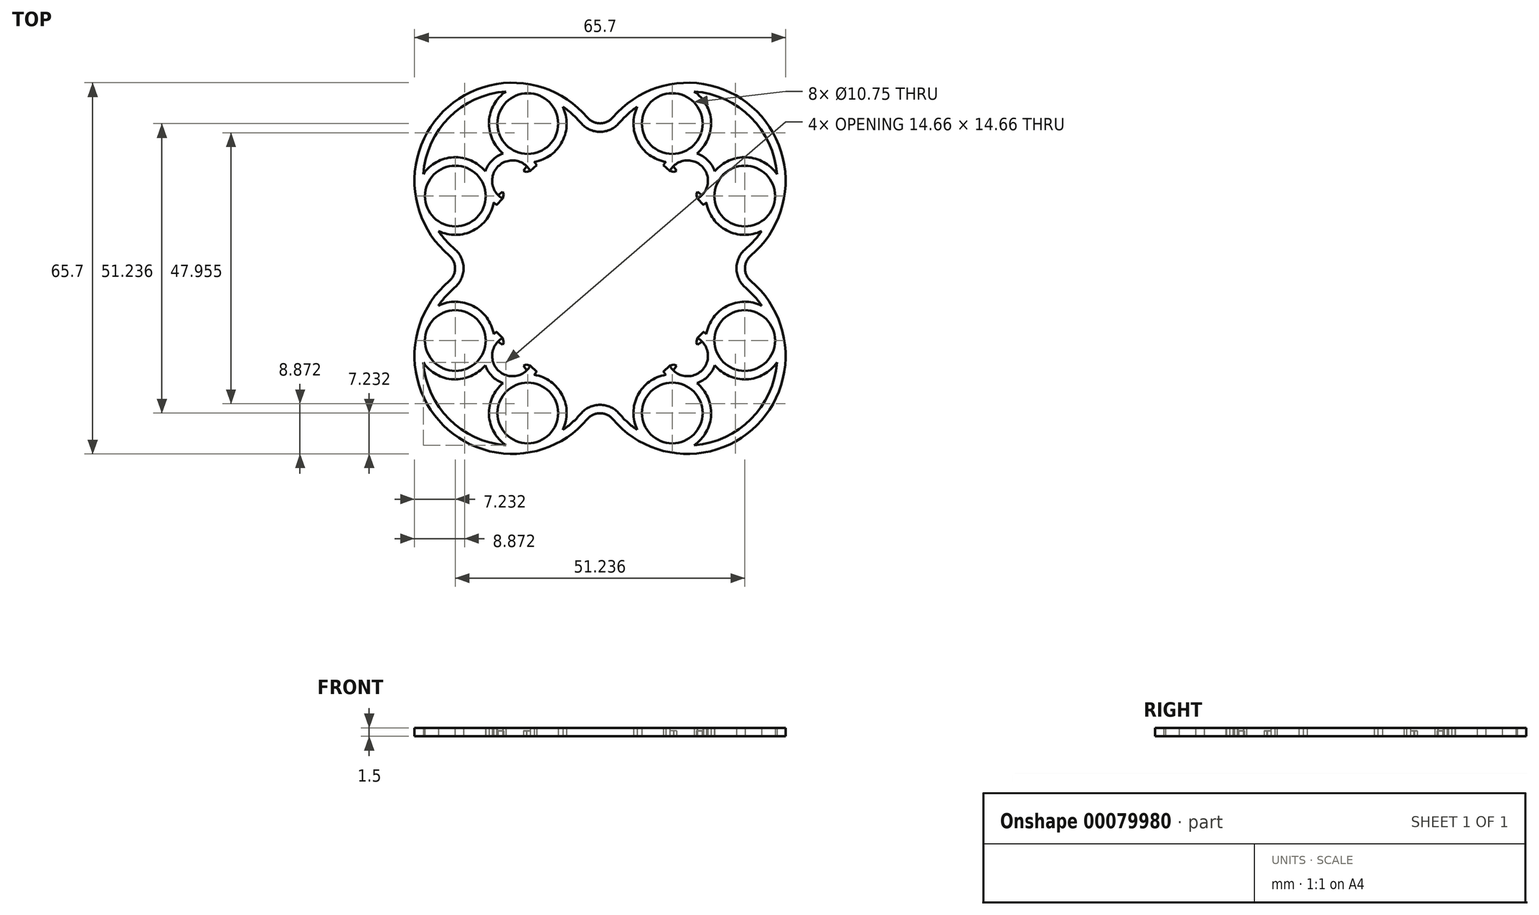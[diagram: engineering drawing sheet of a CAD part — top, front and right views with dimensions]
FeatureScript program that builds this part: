
annotation { "Feature Type Name" : "Feature", "Feature Type Description" : "" }
export const myFeature = defineFeature(function(context is Context, id is Id, definition is map)
    precondition{}
    {
        {
            var Q0;
            Q0=qCreatedBy(makeId("Top.planeOp"),FACE);
            var sketch = newSketch(context, id + "F0", { "sketchPlane" : qUnion([Q0])});
            skLineSegment(sketch, "E0.bottom", {"start": v(-15.5, 15.5) * mm, "end": v(15.5, 15.5) * mm});
            skLineSegment(sketch, "E0.top", {"start": v(-15.5, -15.5) * mm, "end": v(15.5, -15.5) * mm});
            skLineSegment(sketch, "E0.left", {"start": v(-15.5, 15.5) * mm, "end": v(-15.5, -15.5) * mm});
            skLineSegment(sketch, "E0.right", {"start": v(15.5, 15.5) * mm, "end": v(15.5, -15.5) * mm});
            skPoint(sketch, "E0.middle", {"position": v(0, 0) * mm});
            skCircle(sketch, "E1", {"center": v(-15.5, 15.5) * mm, "radius": 15 * mm});
            skCircle(sketch, "E2", {"center": v(15.5, 15.5) * mm, "radius": 15 * mm});
            skCircle(sketch, "E3", {"center": v(-15.5, -15.5) * mm, "radius": 15 * mm});
            skCircle(sketch, "E4", {"center": v(15.5, -15.5) * mm, "radius": 15 * mm});
            skLineSegment(sketch, "E5.bottom", {"start": v(-10, 10) * mm, "end": v(10, 10) * mm});
            skLineSegment(sketch, "E5.top", {"start": v(-10, -10) * mm, "end": v(10, -10) * mm});
            skLineSegment(sketch, "E5.left", {"start": v(-10, 10) * mm, "end": v(-10, -10) * mm});
            skLineSegment(sketch, "E5.right", {"start": v(10, 10) * mm, "end": v(10, -10) * mm});
            skCircle(sketch, "E6", {"center": v(-15.5, 15.5) * mm, "radius": 4.5 * mm});
            skCircle(sketch, "E7", {"center": v(-15.5, 15.5) * mm, "radius": 3.5 * mm});
            skCircle(sketch, "E8", {"center": v(15.5, 15.5) * mm, "radius": 3.5 * mm});
            skCircle(sketch, "E9", {"center": v(15.5, 15.5) * mm, "radius": 4.5 * mm});
            skCircle(sketch, "E10", {"center": v(15.5, -15.5) * mm, "radius": 4.5 * mm});
            skCircle(sketch, "E11", {"center": v(15.5, -15.5) * mm, "radius": 3.5 * mm});
            skCircle(sketch, "E12", {"center": v(-15.5, -15.5) * mm, "radius": 3.5 * mm});
            skCircle(sketch, "E13", {"center": v(-15.5, -15.5) * mm, "radius": 4.5 * mm});
            skLineSegment(sketch, "E14.bottom", {"start": v(-15.5, 15.5) * mm, "end": v(-10.5, 15.5) * mm});
            skLineSegment(sketch, "E14.left", {"start": v(-15.5, 15.5) * mm, "end": v(-15.5, 20.5) * mm});
            skLineSegment(sketch, "E15", {"start": v(-12.32, 18.68) * mm, "end": v(-18.68, 12.32) * mm});
            skLineSegment(sketch, "E16", {"start": v(-17.9, 11.7) * mm, "end": v(-11.7, 17.9) * mm});
            skLineSegment(sketch, "E17", {"start": v(-13.38, 16.22) * mm, "end": v(-14.08, 16.92) * mm});
            skSolve(sketch);
        }
        {
            var Q0;
            {var subQ1=sQuery(id+"F0.wireOp",EDGE,"E0.bottom");var subQ5=sQuery(id+"F0.wireOp",EDGE,"E14.bottom");var subQ6=makeQuery(id+"F0.imprint","INTERSECT",VERTEX,{"derivedFrom":[subQ1,subQ5]});Q0=makeQuery(id+"F0.imprint","IMPRINT",FACE,{"disambiguationData":[TD([[makeQuery(id+"F0.imprint","IMPRINT",EDGE,{"disambiguationData":[TD([[subQ6,-1.0]])],"derivedFrom":subQ1}),1.0]])]});}
            var sketch = newSketch(context, id + "F1", { "sketchPlane" : qUnion([Q0])});
            skLineSegment(sketch, "E18", {"start": v(-17.05, 13.08) * mm, "end": v(-17.24, 13.54) * mm});
            skLineSegment(sketch, "E19", {"start": v(-17.24, 13.54) * mm, "end": v(-18.05, 12.95) * mm});
            skPoint(sketch, "E20.center", {"position": v(0, 0) * mm});
            skLineSegment(sketch, "E21", {"start": v(-17.25, 12.35) * mm, "end": v(-17.05, 13.08) * mm});
            skArc(sketch, "E22", {"start": v(-12.95, 18.05) * mm, "mid": v(-18.05, 18.05) * mm, "end": v(-18.05, 12.95) * mm});
            skLineSegment(sketch, "E23.0", {"start": v(-17.9, 11.7) * mm, "end": v(-11.7, 17.9) * mm, "construction": true});
            skLineSegment(sketch, "E24", {"start": v(-12.95, 18.05) * mm, "end": v(-13.54, 17.24) * mm});
            skLineSegment(sketch, "E25", {"start": v(-13.54, 17.24) * mm, "end": v(-13.08, 17.05) * mm});
            skLineSegment(sketch, "E26", {"start": v(-13.08, 17.05) * mm, "end": v(-12.35, 17.25) * mm});
            skLineSegment(sketch, "E27", {"start": v(-12.35, 17.25) * mm, "end": v(-11.7, 17.9) * mm, "construction": true});
            skLineSegment(sketch, "E28", {"start": v(-12.35, 17.25) * mm, "end": v(-11.23, 18.3) * mm});
            skArc(sketch, "E29", {"start": v(-3.4, 25.74) * mm, "mid": v(-4.9, 27.29) * mm, "end": v(-6.6, 28.62) * mm});
            skArc(sketch, "E30", {"start": v(-2.26, 26.7) * mm, "mid": v(-27.77, 27.77) * mm, "end": v(-26.7, 2.26) * mm});
            skPoint(sketch, "E31.0", {"position": v(-10, 10) * mm});
            skCircle(sketch, "E32", {"center": v(-12.79, 25.62) * mm, "radius": 5.38 * mm});
            skCircle(sketch, "E33", {"center": v(-25.62, 12.79) * mm, "radius": 5.37 * mm});
            skArc(sketch, "E34", {"start": v(-11.64, 18.84) * mm, "mid": v(-6.68, 22.47) * mm, "end": v(-6.6, 28.62) * mm});
            skArc(sketch, "E35", {"start": v(-20.32, 17.17) * mm, "mid": v(-25.94, 19.66) * mm, "end": v(-31.3, 16.65) * mm});
            skArc(sketch, "E36", {"start": v(-11.23, 18.3) * mm, "mid": v(-11.43, 18.57) * mm, "end": v(-11.64, 18.84) * mm});
            skLineSegment(sketch, "E37", {"start": v(-17.25, 12.35) * mm, "end": v(-18.3, 11.23) * mm});
            skArc(sketch, "E38.trimOffspring", {"start": v(-17.17, 20.32) * mm, "mid": v(-19.1, 19.1) * mm, "end": v(-20.32, 17.17) * mm});
            skArc(sketch, "E39.trimOffspring", {"start": v(-18.84, 11.64) * mm, "mid": v(-18.57, 11.43) * mm, "end": v(-18.3, 11.23) * mm});
            skArc(sketch, "E40.trimOffspring", {"start": v(-16.65, 31.3) * mm, "mid": v(-26.7, 26.7) * mm, "end": v(-31.3, 16.65) * mm});
            skArc(sketch, "E41.trimOffspring", {"start": v(-16.65, 31.3) * mm, "mid": v(-19.66, 25.94) * mm, "end": v(-17.17, 20.32) * mm});
            skArc(sketch, "E42.trimOffspring", {"start": v(-28.62, 6.6) * mm, "mid": v(-22.47, 6.68) * mm, "end": v(-18.84, 11.64) * mm});
            skArc(sketch, "E43.trimOffspring", {"start": v(-28.62, 6.6) * mm, "mid": v(-27.29, 4.9) * mm, "end": v(-25.74, 3.4) * mm});
            skArc(sketch, "E44.1.0", {"start": v(-25.74, -3.4) * mm, "mid": v(-27.29, -4.9) * mm, "end": v(-28.62, -6.6) * mm});
            skArc(sketch, "E44.1.1", {"start": v(-18.84, -11.64) * mm, "mid": v(-22.47, -6.68) * mm, "end": v(-28.62, -6.6) * mm});
            skArc(sketch, "E44.1.2", {"start": v(-18.05, -12.95) * mm, "mid": v(-18.05, -18.05) * mm, "end": v(-12.95, -18.05) * mm});
            skCircle(sketch, "E44.1.3", {"center": v(-25.62, -12.79) * mm, "radius": 5.38 * mm});
            skArc(sketch, "E44.1.4", {"start": v(-17.17, -20.32) * mm, "mid": v(-19.66, -25.94) * mm, "end": v(-16.65, -31.3) * mm});
            skArc(sketch, "E44.1.5", {"start": v(-26.7, -2.26) * mm, "mid": v(-27.77, -27.77) * mm, "end": v(-2.26, -26.7) * mm});
            skArc(sketch, "E44.1.6", {"start": v(-31.3, -16.65) * mm, "mid": v(-26.7, -26.7) * mm, "end": v(-16.65, -31.3) * mm});
            skArc(sketch, "E44.1.7", {"start": v(-6.6, -28.62) * mm, "mid": v(-6.68, -22.47) * mm, "end": v(-11.64, -18.84) * mm});
            skCircle(sketch, "E44.1.8", {"center": v(-12.79, -25.62) * mm, "radius": 5.37 * mm});
            skArc(sketch, "E44.1.9", {"start": v(-31.3, -16.65) * mm, "mid": v(-25.94, -19.66) * mm, "end": v(-20.32, -17.17) * mm});
            skPoint(sketch, "E44.1.10", {"position": v(-10, -10) * mm});
            skArc(sketch, "E44.1.12", {"start": v(-6.6, -28.62) * mm, "mid": v(-4.9, -27.29) * mm, "end": v(-3.4, -25.74) * mm});
            skArc(sketch, "E44.1.14", {"start": v(-20.32, -17.17) * mm, "mid": v(-19.1, -19.1) * mm, "end": v(-17.17, -20.32) * mm});
            skArc(sketch, "E44.1.17", {"start": v(-11.64, -18.84) * mm, "mid": v(-11.43, -18.57) * mm, "end": v(-11.23, -18.3) * mm});
            skArc(sketch, "E44.1.18", {"start": v(-18.3, -11.23) * mm, "mid": v(-18.57, -11.43) * mm, "end": v(-18.84, -11.64) * mm});
            skLineSegment(sketch, "E44.1.19", {"start": v(-12.35, -17.25) * mm, "end": v(-11.23, -18.3) * mm});
            skLineSegment(sketch, "E44.1.20", {"start": v(-12.35, -17.25) * mm, "end": v(-13.08, -17.05) * mm});
            skLineSegment(sketch, "E44.1.21", {"start": v(-18.05, -12.95) * mm, "end": v(-17.24, -13.54) * mm});
            skLineSegment(sketch, "E44.1.22", {"start": v(-17.05, -13.08) * mm, "end": v(-17.25, -12.35) * mm});
            skLineSegment(sketch, "E44.1.23", {"start": v(-13.08, -17.05) * mm, "end": v(-13.54, -17.24) * mm});
            skLineSegment(sketch, "E44.1.24", {"start": v(-13.54, -17.24) * mm, "end": v(-12.95, -18.05) * mm});
            skLineSegment(sketch, "E44.1.25", {"start": v(-17.24, -13.54) * mm, "end": v(-17.05, -13.08) * mm});
            skLineSegment(sketch, "E44.1.26", {"start": v(-17.25, -12.35) * mm, "end": v(-18.3, -11.23) * mm});
            skLineSegment(sketch, "E44.1.27", {"start": v(-17.25, -12.35) * mm, "end": v(-17.9, -11.7) * mm, "construction": true});
            skArc(sketch, "E44.2.0", {"start": v(3.4, -25.74) * mm, "mid": v(4.9, -27.29) * mm, "end": v(6.6, -28.62) * mm});
            skArc(sketch, "E44.2.1", {"start": v(11.64, -18.84) * mm, "mid": v(6.68, -22.47) * mm, "end": v(6.6, -28.62) * mm});
            skArc(sketch, "E44.2.2", {"start": v(12.95, -18.05) * mm, "mid": v(18.05, -18.05) * mm, "end": v(18.05, -12.95) * mm});
            skCircle(sketch, "E44.2.3", {"center": v(12.79, -25.62) * mm, "radius": 5.38 * mm});
            skArc(sketch, "E44.2.4", {"start": v(20.32, -17.17) * mm, "mid": v(25.94, -19.66) * mm, "end": v(31.3, -16.65) * mm});
            skArc(sketch, "E44.2.6", {"start": v(16.65, -31.3) * mm, "mid": v(26.7, -26.7) * mm, "end": v(31.3, -16.65) * mm});
            skArc(sketch, "E44.2.7", {"start": v(28.62, -6.6) * mm, "mid": v(22.47, -6.68) * mm, "end": v(18.84, -11.64) * mm});
            skCircle(sketch, "E44.2.8", {"center": v(25.62, -12.79) * mm, "radius": 5.37 * mm});
            skArc(sketch, "E44.2.9", {"start": v(16.65, -31.3) * mm, "mid": v(19.66, -25.94) * mm, "end": v(17.17, -20.32) * mm});
            skPoint(sketch, "E44.2.10", {"position": v(10, -10) * mm});
            skArc(sketch, "E44.2.12", {"start": v(28.62, -6.6) * mm, "mid": v(27.29, -4.9) * mm, "end": v(25.74, -3.4) * mm});
            skArc(sketch, "E44.2.14", {"start": v(17.17, -20.32) * mm, "mid": v(19.1, -19.1) * mm, "end": v(20.32, -17.17) * mm});
            skArc(sketch, "E44.2.17", {"start": v(18.84, -11.64) * mm, "mid": v(18.57, -11.43) * mm, "end": v(18.3, -11.23) * mm});
            skArc(sketch, "E44.2.18", {"start": v(11.23, -18.3) * mm, "mid": v(11.43, -18.57) * mm, "end": v(11.64, -18.84) * mm});
            skLineSegment(sketch, "E44.2.19", {"start": v(17.25, -12.35) * mm, "end": v(18.3, -11.23) * mm});
            skLineSegment(sketch, "E44.2.20", {"start": v(17.25, -12.35) * mm, "end": v(17.05, -13.08) * mm});
            skLineSegment(sketch, "E44.2.21", {"start": v(12.95, -18.05) * mm, "end": v(13.54, -17.24) * mm});
            skLineSegment(sketch, "E44.2.22", {"start": v(13.08, -17.05) * mm, "end": v(12.35, -17.25) * mm});
            skLineSegment(sketch, "E44.2.23", {"start": v(17.05, -13.08) * mm, "end": v(17.24, -13.54) * mm});
            skLineSegment(sketch, "E44.2.24", {"start": v(17.24, -13.54) * mm, "end": v(18.05, -12.95) * mm});
            skLineSegment(sketch, "E44.2.25", {"start": v(13.54, -17.24) * mm, "end": v(13.08, -17.05) * mm});
            skLineSegment(sketch, "E44.2.26", {"start": v(12.35, -17.25) * mm, "end": v(11.23, -18.3) * mm});
            skLineSegment(sketch, "E44.2.27", {"start": v(12.35, -17.25) * mm, "end": v(11.7, -17.9) * mm, "construction": true});
            skArc(sketch, "E44.3.0", {"start": v(25.74, 3.4) * mm, "mid": v(27.29, 4.9) * mm, "end": v(28.62, 6.6) * mm});
            skArc(sketch, "E44.3.1", {"start": v(18.84, 11.64) * mm, "mid": v(22.47, 6.68) * mm, "end": v(28.62, 6.6) * mm});
            skArc(sketch, "E44.3.2", {"start": v(18.05, 12.95) * mm, "mid": v(18.05, 18.05) * mm, "end": v(12.95, 18.05) * mm});
            skCircle(sketch, "E44.3.3", {"center": v(25.62, 12.79) * mm, "radius": 5.38 * mm});
            skArc(sketch, "E44.3.4", {"start": v(17.17, 20.32) * mm, "mid": v(19.66, 25.94) * mm, "end": v(16.65, 31.3) * mm});
            skArc(sketch, "E44.3.5", {"start": v(26.7, 2.26) * mm, "mid": v(27.77, 27.77) * mm, "end": v(2.26, 26.7) * mm});
            skArc(sketch, "E44.3.6", {"start": v(31.3, 16.65) * mm, "mid": v(26.7, 26.7) * mm, "end": v(16.65, 31.3) * mm});
            skArc(sketch, "E44.3.7", {"start": v(6.6, 28.62) * mm, "mid": v(6.68, 22.47) * mm, "end": v(11.64, 18.84) * mm});
            skCircle(sketch, "E44.3.8", {"center": v(12.79, 25.62) * mm, "radius": 5.37 * mm});
            skArc(sketch, "E44.3.9", {"start": v(31.3, 16.65) * mm, "mid": v(25.94, 19.66) * mm, "end": v(20.32, 17.17) * mm});
            skPoint(sketch, "E44.3.10", {"position": v(10, 10) * mm});
            skArc(sketch, "E44.3.12", {"start": v(6.6, 28.62) * mm, "mid": v(4.9, 27.29) * mm, "end": v(3.4, 25.74) * mm});
            skArc(sketch, "E44.3.14", {"start": v(20.32, 17.17) * mm, "mid": v(19.1, 19.1) * mm, "end": v(17.17, 20.32) * mm});
            skArc(sketch, "E44.3.17", {"start": v(11.64, 18.84) * mm, "mid": v(11.43, 18.57) * mm, "end": v(11.23, 18.3) * mm});
            skArc(sketch, "E44.3.18", {"start": v(18.3, 11.23) * mm, "mid": v(18.57, 11.43) * mm, "end": v(18.84, 11.64) * mm});
            skLineSegment(sketch, "E44.3.19", {"start": v(12.35, 17.25) * mm, "end": v(11.23, 18.3) * mm});
            skLineSegment(sketch, "E44.3.20", {"start": v(12.35, 17.25) * mm, "end": v(13.08, 17.05) * mm});
            skLineSegment(sketch, "E44.3.21", {"start": v(18.05, 12.95) * mm, "end": v(17.24, 13.54) * mm});
            skLineSegment(sketch, "E44.3.22", {"start": v(17.05, 13.08) * mm, "end": v(17.25, 12.35) * mm});
            skLineSegment(sketch, "E44.3.23", {"start": v(13.08, 17.05) * mm, "end": v(13.54, 17.24) * mm});
            skLineSegment(sketch, "E44.3.24", {"start": v(13.54, 17.24) * mm, "end": v(12.95, 18.05) * mm});
            skLineSegment(sketch, "E44.3.25", {"start": v(17.24, 13.54) * mm, "end": v(17.05, 13.08) * mm});
            skLineSegment(sketch, "E44.3.26", {"start": v(17.25, 12.35) * mm, "end": v(18.3, 11.23) * mm});
            skLineSegment(sketch, "E44.3.27", {"start": v(17.25, 12.35) * mm, "end": v(17.9, 11.7) * mm, "construction": true});
            skArc(sketch, "E45", {"start": v(-3.4, 25.74) * mm, "mid": v(0, 24.16) * mm, "end": v(3.4, 25.74) * mm});
            skArc(sketch, "E46", {"start": v(-2.26, 26.7) * mm, "mid": v(0, 25.66) * mm, "end": v(2.26, 26.7) * mm});
            skArc(sketch, "E47.1.0", {"start": v(-26.7, -2.26) * mm, "mid": v(-25.66, 0) * mm, "end": v(-26.7, 2.26) * mm});
            skArc(sketch, "E47.1.1", {"start": v(-25.74, -3.4) * mm, "mid": v(-24.16, 0) * mm, "end": v(-25.74, 3.4) * mm});
            skArc(sketch, "E47.2.0", {"start": v(2.26, -26.7) * mm, "mid": v(0, -25.66) * mm, "end": v(-2.26, -26.7) * mm});
            skArc(sketch, "E47.2.1", {"start": v(3.4, -25.74) * mm, "mid": v(0, -24.16) * mm, "end": v(-3.4, -25.74) * mm});
            skArc(sketch, "E47.3.0", {"start": v(26.7, 2.26) * mm, "mid": v(25.66, 0) * mm, "end": v(26.7, -2.26) * mm});
            skArc(sketch, "E47.3.1", {"start": v(25.74, 3.4) * mm, "mid": v(24.16, 0) * mm, "end": v(25.74, -3.4) * mm});
            skArc(sketch, "E48.trimOffspring", {"start": v(2.26, -26.7) * mm, "mid": v(27.77, -27.77) * mm, "end": v(26.7, -2.26) * mm});
            skSolve(sketch);
        }
        {
            var Q0;
            Q0 = qSketchRegion(id + "F1", true);
            extrude(context, id + "F2", {"entities" : qUnion([Q0]), "depth" : 1.5 * mm});
        }
        {
            var Q0;
            Q0=makeQuery(id+"F2.opExtrude","CAP_FACE",FACE,{"disambiguationData":[OSD([sQuery(id+"F1.wireOp",EDGE,"E18"),sQuery(id+"F1.wireOp",EDGE,"E19"),sQuery(id+"F1.wireOp",EDGE,"E21"),sQuery(id+"F1.wireOp",EDGE,"E22"),sQuery(id+"F1.wireOp",EDGE,"E24"),sQuery(id+"F1.wireOp",EDGE,"E25"),sQuery(id+"F1.wireOp",EDGE,"E26"),sQuery(id+"F1.wireOp",EDGE,"E28"),sQuery(id+"F1.wireOp",EDGE,"E29"),sQuery(id+"F1.wireOp",EDGE,"E30"),sQuery(id+"F1.wireOp",EDGE,"E32"),sQuery(id+"F1.wireOp",EDGE,"E33"),sQuery(id+"F1.wireOp",EDGE,"E34"),sQuery(id+"F1.wireOp",EDGE,"E35"),sQuery(id+"F1.wireOp",EDGE,"E36"),sQuery(id+"F1.wireOp",EDGE,"E37"),sQuery(id+"F1.wireOp",EDGE,"E38.trimOffspring"),sQuery(id+"F1.wireOp",EDGE,"E39.trimOffspring"),sQuery(id+"F1.wireOp",EDGE,"E40.trimOffspring"),sQuery(id+"F1.wireOp",EDGE,"E41.trimOffspring"),sQuery(id+"F1.wireOp",EDGE,"E42.trimOffspring"),sQuery(id+"F1.wireOp",EDGE,"E43.trimOffspring"),sQuery(id+"F1.wireOp",EDGE,"E44.1.0"),sQuery(id+"F1.wireOp",EDGE,"E44.1.1"),sQuery(id+"F1.wireOp",EDGE,"E44.1.2"),sQuery(id+"F1.wireOp",EDGE,"E44.1.3"),sQuery(id+"F1.wireOp",EDGE,"E44.1.4"),sQuery(id+"F1.wireOp",EDGE,"E44.1.5"),sQuery(id+"F1.wireOp",EDGE,"E44.1.6"),sQuery(id+"F1.wireOp",EDGE,"E44.1.7"),sQuery(id+"F1.wireOp",EDGE,"E44.1.8"),sQuery(id+"F1.wireOp",EDGE,"E44.1.9"),sQuery(id+"F1.wireOp",EDGE,"E44.1.12"),sQuery(id+"F1.wireOp",EDGE,"E44.1.14"),sQuery(id+"F1.wireOp",EDGE,"E44.1.17"),sQuery(id+"F1.wireOp",EDGE,"E44.1.18"),sQuery(id+"F1.wireOp",EDGE,"E44.1.19"),sQuery(id+"F1.wireOp",EDGE,"E44.1.20"),sQuery(id+"F1.wireOp",EDGE,"E44.1.21"),sQuery(id+"F1.wireOp",EDGE,"E44.1.22"),sQuery(id+"F1.wireOp",EDGE,"E44.1.23"),sQuery(id+"F1.wireOp",EDGE,"E44.1.24"),sQuery(id+"F1.wireOp",EDGE,"E44.1.25"),sQuery(id+"F1.wireOp",EDGE,"E44.1.26"),sQuery(id+"F1.wireOp",EDGE,"E44.2.0"),sQuery(id+"F1.wireOp",EDGE,"E44.2.1"),sQuery(id+"F1.wireOp",EDGE,"E44.2.2"),sQuery(id+"F1.wireOp",EDGE,"E44.2.3"),sQuery(id+"F1.wireOp",EDGE,"E44.2.4"),sQuery(id+"F1.wireOp",EDGE,"E44.2.6"),sQuery(id+"F1.wireOp",EDGE,"E44.2.7"),sQuery(id+"F1.wireOp",EDGE,"E44.2.8"),sQuery(id+"F1.wireOp",EDGE,"E44.2.9"),sQuery(id+"F1.wireOp",EDGE,"E44.2.12"),sQuery(id+"F1.wireOp",EDGE,"E44.2.14"),sQuery(id+"F1.wireOp",EDGE,"E44.2.17"),sQuery(id+"F1.wireOp",EDGE,"E44.2.18"),sQuery(id+"F1.wireOp",EDGE,"E44.2.19"),sQuery(id+"F1.wireOp",EDGE,"E44.2.20"),sQuery(id+"F1.wireOp",EDGE,"E44.2.21"),sQuery(id+"F1.wireOp",EDGE,"E44.2.22"),sQuery(id+"F1.wireOp",EDGE,"E44.2.23"),sQuery(id+"F1.wireOp",EDGE,"E44.2.24"),sQuery(id+"F1.wireOp",EDGE,"E44.2.25"),sQuery(id+"F1.wireOp",EDGE,"E44.2.26"),sQuery(id+"F1.wireOp",EDGE,"E44.3.0"),sQuery(id+"F1.wireOp",EDGE,"E44.3.1"),sQuery(id+"F1.wireOp",EDGE,"E44.3.2"),sQuery(id+"F1.wireOp",EDGE,"E44.3.3"),sQuery(id+"F1.wireOp",EDGE,"E44.3.4"),sQuery(id+"F1.wireOp",EDGE,"E44.3.5"),sQuery(id+"F1.wireOp",EDGE,"E44.3.6"),sQuery(id+"F1.wireOp",EDGE,"E44.3.7"),sQuery(id+"F1.wireOp",EDGE,"E44.3.8"),sQuery(id+"F1.wireOp",EDGE,"E44.3.9"),sQuery(id+"F1.wireOp",EDGE,"E44.3.12"),sQuery(id+"F1.wireOp",EDGE,"E44.3.14"),sQuery(id+"F1.wireOp",EDGE,"E44.3.17"),sQuery(id+"F1.wireOp",EDGE,"E44.3.18"),sQuery(id+"F1.wireOp",EDGE,"E44.3.19"),sQuery(id+"F1.wireOp",EDGE,"E44.3.20"),sQuery(id+"F1.wireOp",EDGE,"E44.3.21"),sQuery(id+"F1.wireOp",EDGE,"E44.3.22"),sQuery(id+"F1.wireOp",EDGE,"E44.3.23"),sQuery(id+"F1.wireOp",EDGE,"E44.3.24"),sQuery(id+"F1.wireOp",EDGE,"E44.3.25"),sQuery(id+"F1.wireOp",EDGE,"E44.3.26"),sQuery(id+"F1.wireOp",EDGE,"E45"),sQuery(id+"F1.wireOp",EDGE,"E46"),sQuery(id+"F1.wireOp",EDGE,"E47.1.0"),sQuery(id+"F1.wireOp",EDGE,"E47.1.1"),sQuery(id+"F1.wireOp",EDGE,"E47.2.0"),sQuery(id+"F1.wireOp",EDGE,"E47.2.1"),sQuery(id+"F1.wireOp",EDGE,"E47.3.0"),sQuery(id+"F1.wireOp",EDGE,"E47.3.1"),sQuery(id+"F1.wireOp",EDGE,"E48.trimOffspring")])],"isStart":false});
            var sketch = newSketch(context, id + "F3", { "sketchPlane" : qUnion([Q0])});
            skPoint(sketch, "E49.0", {"position": v(-15.5, 15.5) * mm});
            skCircle(sketch, "E50", {"center": v(-15.5, 15.5) * mm, "radius": 3.6 * mm});
            skCircle(sketch, "E51.1.0", {"center": v(-15.5, -15.5) * mm, "radius": 3.6 * mm});
            skCircle(sketch, "E51.2.0", {"center": v(15.5, -15.5) * mm, "radius": 3.6 * mm});
            skCircle(sketch, "E51.3.0", {"center": v(15.5, 15.5) * mm, "radius": 3.6 * mm});
            skPoint(sketch, "E51.center", {"position": v(0, 0) * mm});
            skSolve(sketch);
        }
        {
            var Q0;
            Q0 = qSketchRegion(id + "F3", true);
            extrude(context, id + "F4", {"entities" : qUnion([Q0]), "operationType" : NewBodyOperationType.REMOVE, "oppositeDirection" : true, "depth" : 0.5 * mm});
        }
    });
